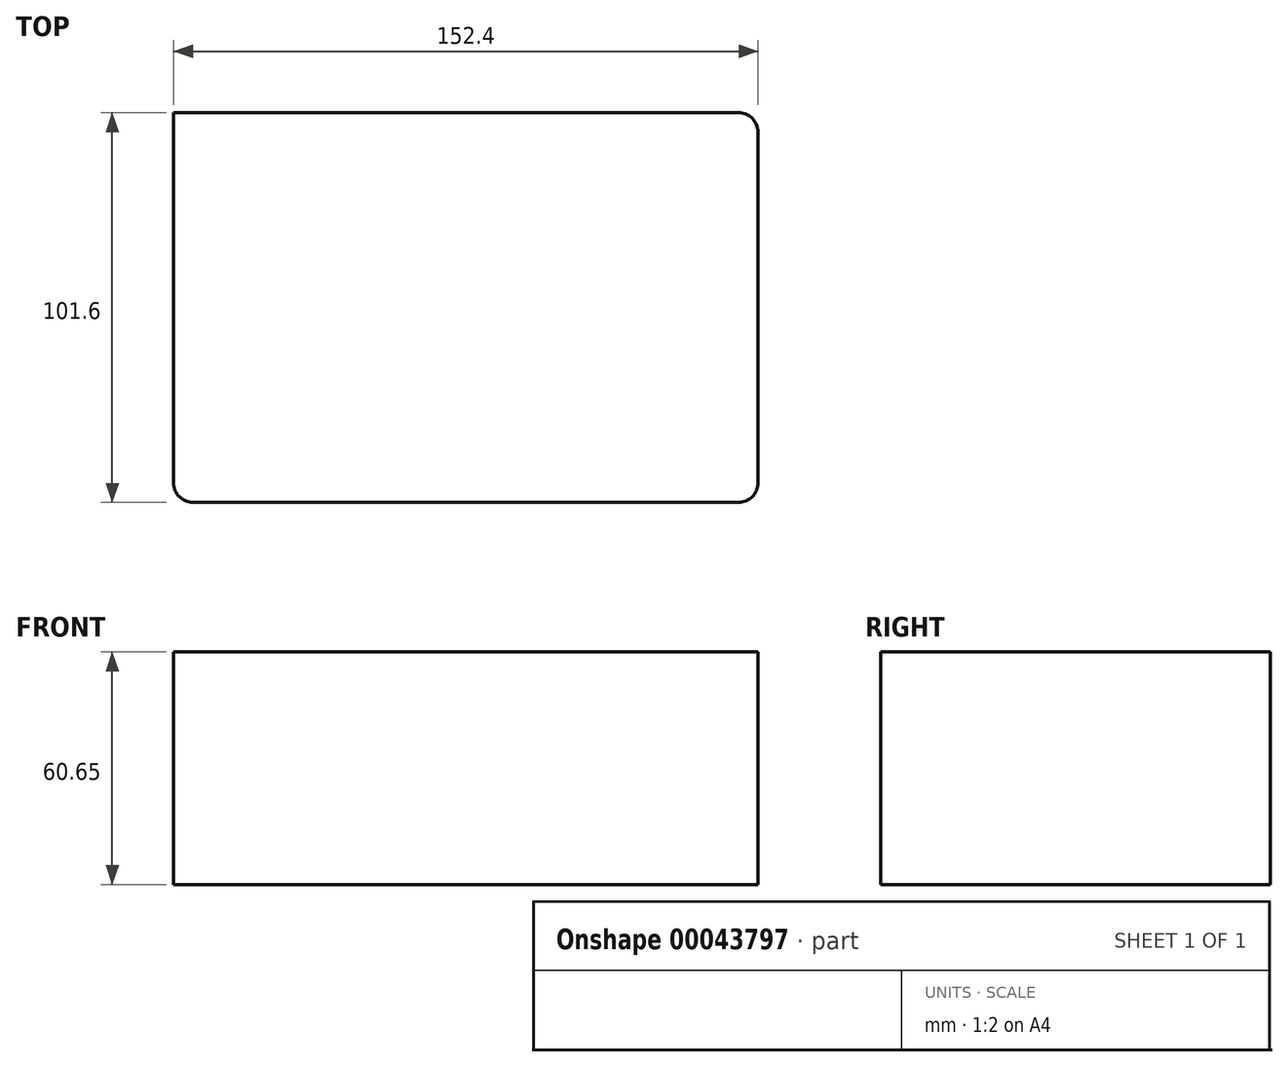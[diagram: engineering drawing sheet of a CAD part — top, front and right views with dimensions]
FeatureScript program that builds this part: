
annotation { "Feature Type Name" : "Feature", "Feature Type Description" : "" }
export const myFeature = defineFeature(function(context is Context, id is Id, definition is map)
    precondition{}
    {
        {
            var Q0;
            Q0=qCreatedBy(makeId("Top.planeOp"),FACE);
            var sketch = newSketch(context, id + "F0", { "sketchPlane" : qUnion([Q0])});
            skLineSegment(sketch, "E0.rect.bottom", {"start": v(108.85, 0) * mm, "end": v(-43.55, 0) * mm});
            skLineSegment(sketch, "E0.rect.top", {"start": v(108.85, 101.6) * mm, "end": v(-43.55, 101.6) * mm});
            skLineSegment(sketch, "E0.rect.left", {"start": v(108.85, 0) * mm, "end": v(108.85, 101.6) * mm});
            skLineSegment(sketch, "E0.rect.right", {"start": v(-43.55, 0) * mm, "end": v(-43.55, 101.6) * mm});
            skPoint(sketch, "E0.rect.middle", {"position": v(32.65, 50.8) * mm});
            skSolve(sketch);
        }
        {
            var Q0;
            Q0=makeQuery(id+"F0.imprint","IMPRINT",FACE,{"disambiguationData":[TD([[makeQuery(id+"F0.imprint","IMPRINT",EDGE,{"derivedFrom":sQuery(id+"F0.wireOp",EDGE,"E0.rect.bottom")}),-1.0]])]});
            extrude(context, id + "F1", {"entities" : qUnion([Q0]), "depth" : 60.65 * mm});
        }
        {
            var Q0;
            Q0=makeQuery(id+"F1.opExtrude","SWEPT_EDGE",EDGE,{"disambiguationData":[OSD([sQuery(id+"F0.wireOp",EDGE,"E0.rect.bottom"),sQuery(id+"F0.wireOp",EDGE,"E0.rect.left")])]});
            var Q1;
            Q1=makeQuery(id+"F1.opExtrude","SWEPT_EDGE",EDGE,{"disambiguationData":[OSD([sQuery(id+"F0.wireOp",EDGE,"E0.rect.bottom"),sQuery(id+"F0.wireOp",EDGE,"E0.rect.right")])]});
            var Q2;
            Q2=makeQuery(id+"F1.opExtrude","SWEPT_EDGE",EDGE,{"disambiguationData":[OSD([sQuery(id+"F0.wireOp",EDGE,"E0.rect.top"),sQuery(id+"F0.wireOp",EDGE,"E0.rect.left")])]});
            fillet(context, id + "F2", {"entities" : qUnion([Q0, Q1, Q2]), "radius" : 5.08 * mm, "tangentPropagation" : true, "allowEdgeOverflow" : false});
        }
    });
